# Revit family: RN 57021 Optifitt-Press-Réduction
name_source: partatom
category: Rohrformteile
units: mm (PartAtom-declared; Revit-internal decimal feet)

## family parameters
Arbeitsebenenbasiert = Nein
Beim Laden mit Abzugskörper schneiden = Nein
Bemaßung runder Anschluss = Durchmesser verwenden
Gemeinsam genutzt = Nein
Immer vertikal = Ja
OmniClass-Nummer = 23.60.30.11.14
OmniClass-Titel = Pipework Fittings
Teiletyp = Übergang

## types (1)
- Var
    Bauelement = 03.01.07.03
    Beschreibung = Optifitt-Press-Réduction
    Hersteller = R. Nussbaum AG
    IfcDescription = Optifitt-Press-Réduction
    IfcExportAs = IfcPipeFitting
    IfcExportType = TRANSITION
    Modell = 57021.25
    RN_LOD = LOD 400
    RN_Manufactur = R. Nussbaum AG
    RN_Mat = Stahl verzinkt vernickelt
    RN_Serie = Optifitt press
    RN_tab = RN_57021
    Typenkommentare = Optifitt-Press-Réduction Var
    URL = https://www.nussbaum.ch

## geometry (parser evidence)
native form markers: Sweep x1
no freeform markers — native parametric forms only
